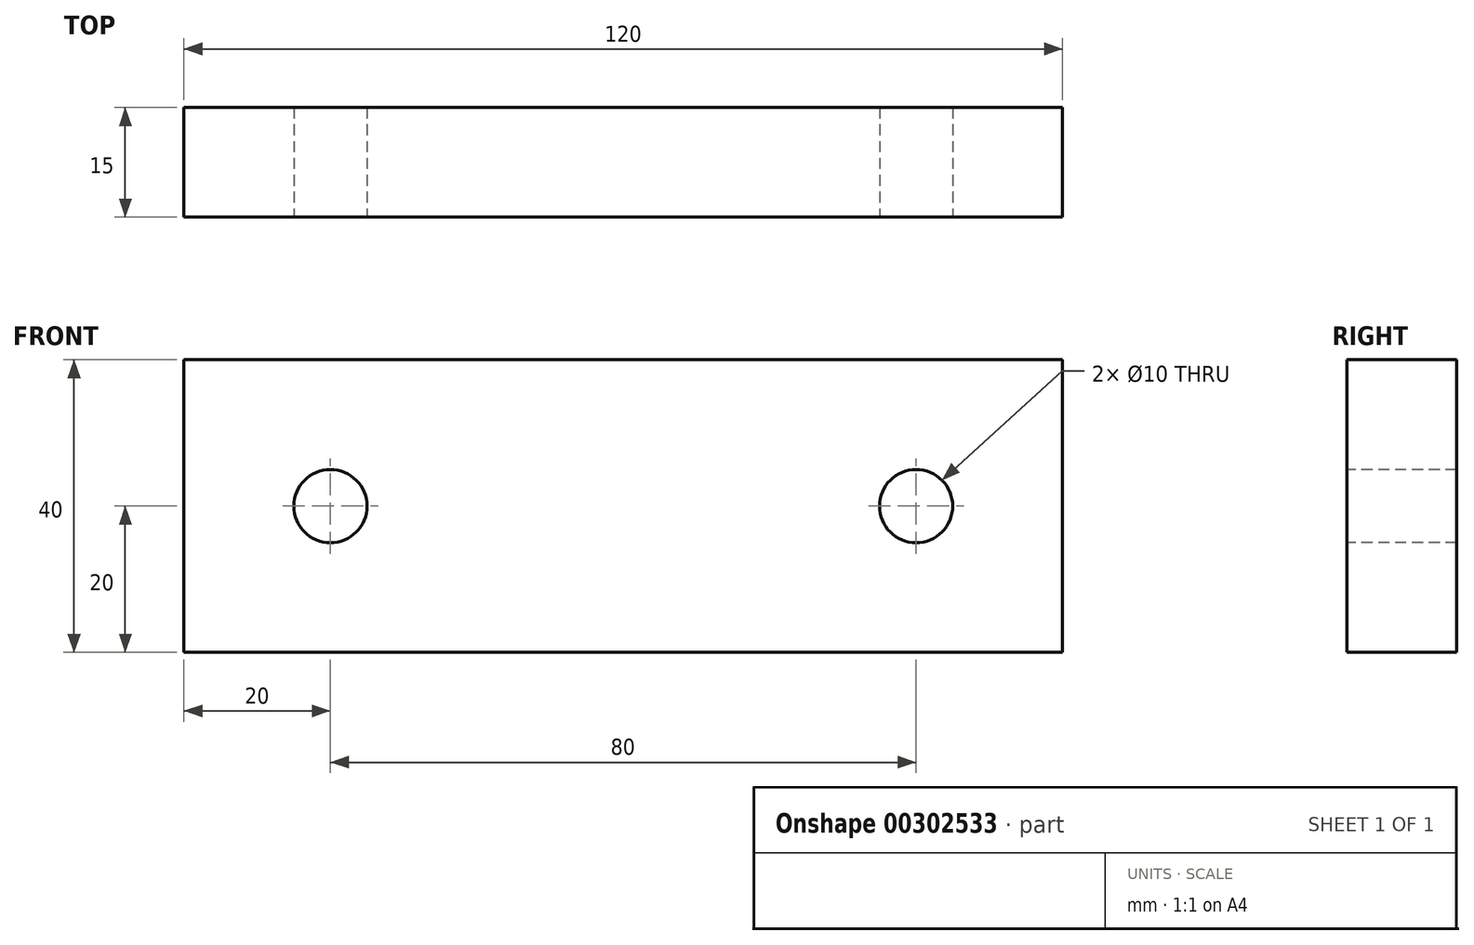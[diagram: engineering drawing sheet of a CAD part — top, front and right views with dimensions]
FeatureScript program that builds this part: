
annotation { "Feature Type Name" : "Feature", "Feature Type Description" : "" }
export const myFeature = defineFeature(function(context is Context, id is Id, definition is map)
    precondition{}
    {
        {
            var Q0;
            Q0=qCreatedBy(makeId("Front.planeOp"),FACE);
            var sketch = newSketch(context, id + "F0", { "sketchPlane" : qUnion([Q0])});
            skLineSegment(sketch, "E0.bottom", {"start": v(0, 0) * mm, "end": v(120, 0) * mm});
            skLineSegment(sketch, "E0.top", {"start": v(0, 40) * mm, "end": v(120, 40) * mm});
            skLineSegment(sketch, "E0.left", {"start": v(0, 0) * mm, "end": v(0, 40) * mm});
            skLineSegment(sketch, "E0.right", {"start": v(120, 0) * mm, "end": v(120, 40) * mm});
            skSolve(sketch);
        }
        {
            var Q0;
            Q0 = qSketchRegion(id + "F0", true);
            extrude(context, id + "F1", {"entities" : qUnion([Q0]), "depth" : 15 * mm});
        }
        {
            var Q0;
            Q0=makeQuery(id+"F1.opExtrude","CAP_FACE",FACE,{"disambiguationData":[OSD([sQuery(id+"F0.wireOp",EDGE,"E0.bottom"),sQuery(id+"F0.wireOp",EDGE,"E0.top"),sQuery(id+"F0.wireOp",EDGE,"E0.left"),sQuery(id+"F0.wireOp",EDGE,"E0.right")])],"isStart":false});
            var sketch = newSketch(context, id + "F2", { "sketchPlane" : qUnion([Q0])});
            skCircle(sketch, "E1", {"center": v(20, 20) * mm, "radius": 5 * mm});
            skCircle(sketch, "E2", {"center": v(100, 20) * mm, "radius": 5 * mm});
            skSolve(sketch);
        }
        {
            var Q0;
            Q0 = qSketchRegion(id + "F2", true);
            extrude(context, id + "F3", {"entities" : qUnion([Q0]), "operationType" : NewBodyOperationType.REMOVE, "oppositeDirection" : true, "depth" : 15 * mm});
        }
    });
